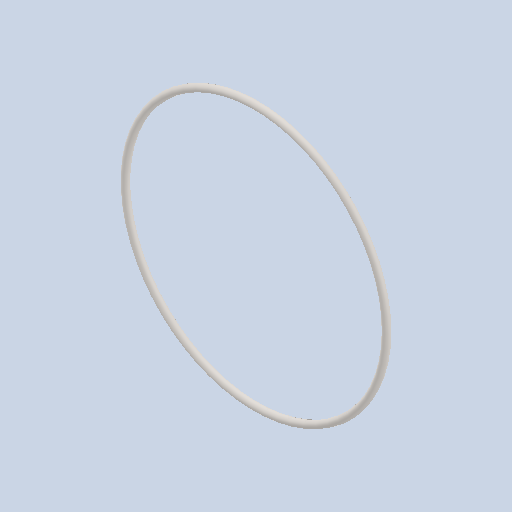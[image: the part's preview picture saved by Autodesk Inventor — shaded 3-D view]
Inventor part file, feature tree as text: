
AUTODESK INVENTOR PART (.ipt)
format: ipt  version: 2024.1 (Build 281209000, 209)  size: 103,936 bytes
history: native  units: in
note: dims shown in document units (in); Inventor stores cm internally (conversion verified against a paired STEP export)
features: sweep x1
ambient origin geometry x8: Origin, YZ Plane, XZ Plane, XY Plane, X Axis, Y Axis, Z Axis, Center Point
bodies: Solid1 (feature_tree)
feature tree (1):
  sweep  "Sweep1"
